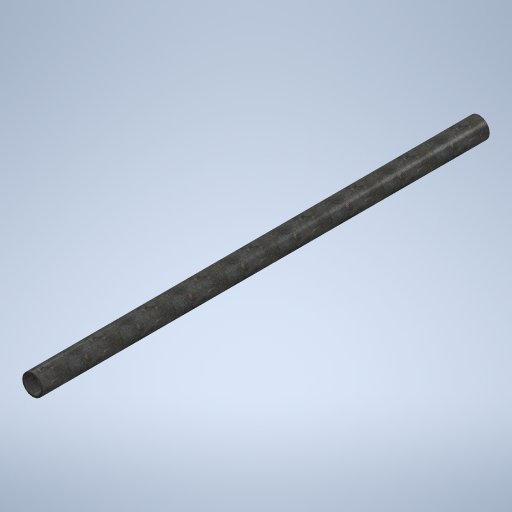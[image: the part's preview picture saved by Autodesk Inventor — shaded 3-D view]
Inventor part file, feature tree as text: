
AUTODESK INVENTOR PART (.ipt)
format: ipt  version: 2024 (Build 280153000, 153)  size: 286,720 bytes
history: native  units: in
note: dims shown in document units (in); Inventor stores cm internally (conversion verified against a paired STEP export)
features: sketch x2, extrude x1
ambient origin geometry x8: Origin, YZ Plane, XZ Plane, XY Plane, X Axis, Y Axis, Z Axis, Center Point
bodies: Solid1 (feature_tree)
feature tree (3):
  sketch  "Sketch1"  dims[d0=2.7559in d1=2.2835in]
  extrude  "Extrusion1"  Depth=2.2835in
  sketch  "Sketch2"  dims[d2=59.0551in d3=0.0in]
